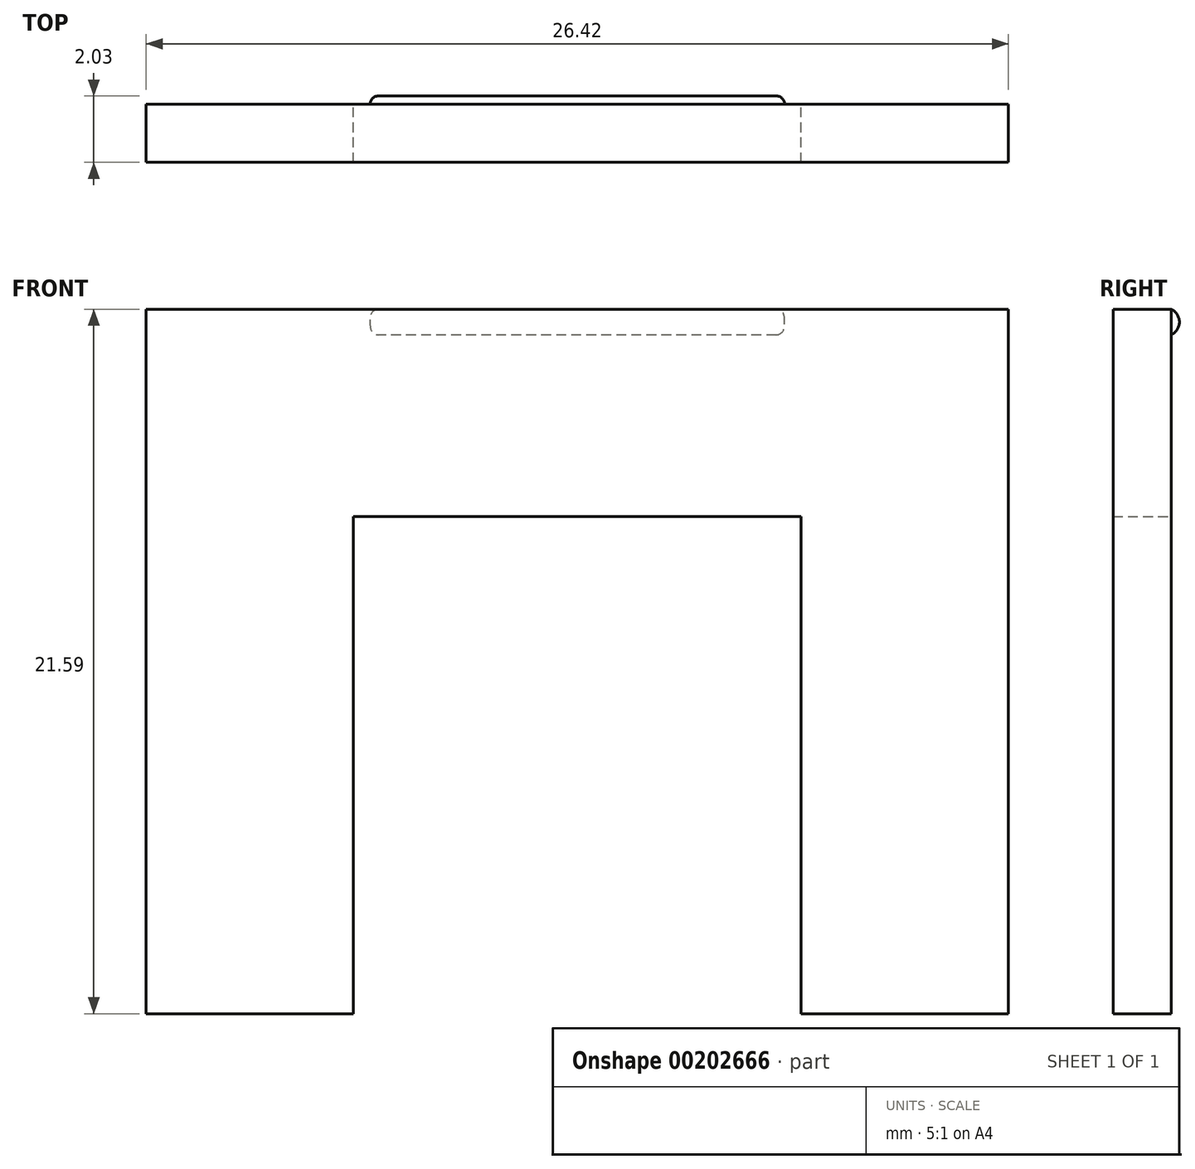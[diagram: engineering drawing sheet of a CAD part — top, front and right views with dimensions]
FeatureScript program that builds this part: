
annotation { "Feature Type Name" : "Feature", "Feature Type Description" : "" }
export const myFeature = defineFeature(function(context is Context, id is Id, definition is map)
    precondition{}
    {
        {
            var Q0;
            Q0=qCreatedBy(makeId("Front.planeOp"),FACE);
            var sketch = newSketch(context, id + "F0", { "sketchPlane" : qUnion([Q0])});
            skLineSegment(sketch, "E0", {"start": v(0, 0) * mm, "end": v(0, 4.37) * mm});
            skLineSegment(sketch, "E1", {"start": v(-6.86, 4.37) * mm, "end": v(6.86, 4.37) * mm});
            skLineSegment(sketch, "E2", {"start": v(-6.86, 4.37) * mm, "end": v(-6.86, -10.87) * mm});
            skLineSegment(sketch, "E3", {"start": v(-6.86, -10.87) * mm, "end": v(-13.2, -10.87) * mm});
            skLineSegment(sketch, "E4", {"start": v(-13.2, -10.87) * mm, "end": v(-13.2, 10.72) * mm});
            skLineSegment(sketch, "E5", {"start": v(-13.2, 10.72) * mm, "end": v(13.2, 10.72) * mm});
            skLineSegment(sketch, "E6", {"start": v(13.2, 10.72) * mm, "end": v(13.2, -10.87) * mm});
            skLineSegment(sketch, "E7", {"start": v(13.2, -10.87) * mm, "end": v(6.86, -10.87) * mm});
            skLineSegment(sketch, "E8", {"start": v(6.86, -10.87) * mm, "end": v(6.86, 4.37) * mm});
            skSolve(sketch);
        }
        {
            var Q0;
            Q0 = qSketchRegion(id + "F0", true);
            extrude(context, id + "F1", {"entities" : qUnion([Q0]), "depth" : 1.78 * mm});
        }
        {
            var Q0;
            Q0=qCreatedBy(makeId("Right.planeOp"),FACE);
            var sketch = newSketch(context, id + "F2", { "sketchPlane" : qUnion([Q0])});
            skLineSegment(sketch, "E9", {"start": v(0, 10.72) * mm, "end": v(0, 7.55) * mm});
            skLineSegment(sketch, "E10", {"start": v(0, 9.93) * mm, "end": v(0, 8.33) * mm});
            skArc(sketch, "E11", {"start": v(0, 9.93) * mm, "mid": v(0.25, 10.33) * mm, "end": v(0, 10.72) * mm});
            skLineSegment(sketch, "E12", {"start": v(-0.18, 10.33) * mm, "end": v(0.25, 10.33) * mm});
            skSolve(sketch);
        }
        {
            var Q0;
            Q0 = qSketchRegion(id + "F2", true);
            extrude(context, id + "F3", {"entities" : qUnion([Q0]), "operationType" : NewBodyOperationType.ADD, "endBound" : BoundingType.SYMMETRIC, "depth" : 12.7 * mm});
        }
        {
            var Q0;
            Q0=makeQuery(id+"F3.opExtrude","CAP_EDGE",EDGE,{"disambiguationData":[OSD([sQuery(id+"F2.wireOp",EDGE,"E11")])],"isStart":true});
            var Q1;
            Q1=makeQuery(id+"F3.opExtrude","CAP_EDGE",EDGE,{"disambiguationData":[OSD([sQuery(id+"F2.wireOp",EDGE,"E11")])],"isStart":false});
            fillet(context, id + "F4", {"entities" : qUnion([Q0, Q1]), "radius" : 0.25 * mm, "tangentPropagation" : true, "allowEdgeOverflow" : false});
        }
    });
